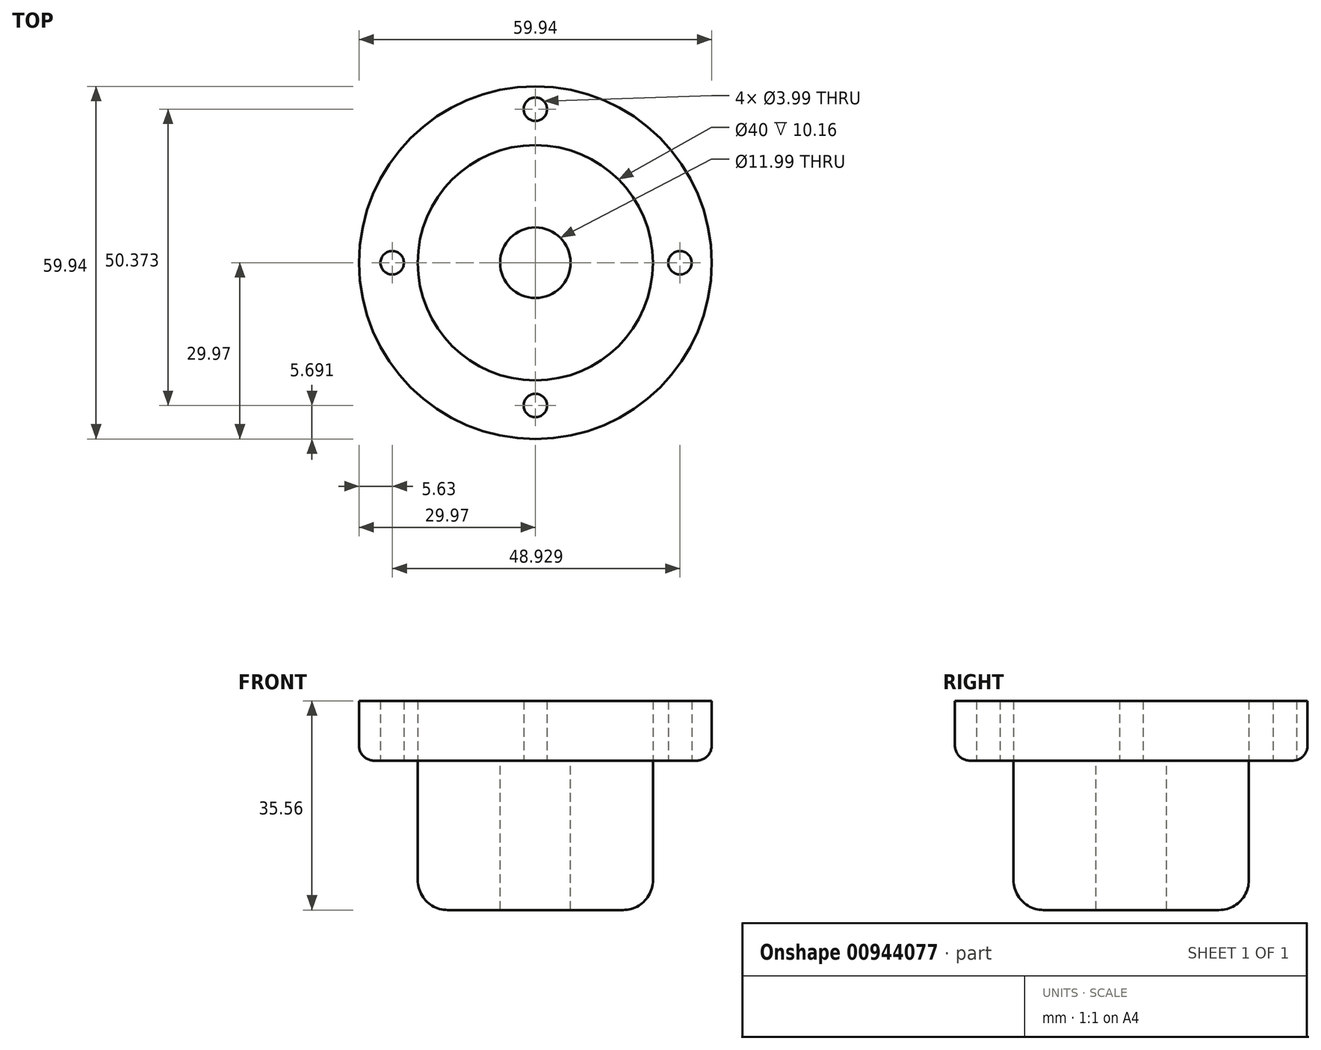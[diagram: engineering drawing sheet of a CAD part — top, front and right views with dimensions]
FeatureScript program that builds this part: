
annotation { "Feature Type Name" : "Feature", "Feature Type Description" : "" }
export const myFeature = defineFeature(function(context is Context, id is Id, definition is map)
    precondition{}
    {
        {
            var Q0;
            Q0=qCreatedBy(makeId("Top.planeOp"),FACE);
            var sketch = newSketch(context, id + "F0", { "sketchPlane" : qUnion([Q0])});
            skCircle(sketch, "E0", {"center": v(0, 0) * mm, "radius": 6 * mm});
            skCircle(sketch, "E1", {"center": v(0, 0) * mm, "radius": 20 * mm});
            skCircle(sketch, "E2", {"center": v(0, 0) * mm, "radius": 29.97 * mm});
            skPoint(sketch, "E3.center.orphan", {"position": v(0, -12.96) * mm});
            skPoint(sketch, "E4.center.orphan", {"position": v(-13.55, 0) * mm});
            skPoint(sketch, "E5.center.orphan", {"position": v(0, 13.55) * mm});
            skPoint(sketch, "E6.center.orphan", {"position": v(12.22, 0) * mm});
            skCircle(sketch, "E7", {"center": v(0, 26.1) * mm, "radius": 2 * mm});
            skCircle(sketch, "E8", {"center": v(24.59, 0) * mm, "radius": 2 * mm});
            skCircle(sketch, "E9", {"center": v(0, -24.28) * mm, "radius": 2 * mm});
            skCircle(sketch, "E10", {"center": v(-24.34, 0) * mm, "radius": 2 * mm});
            skSolve(sketch);
        }
        {
            var Q0;
            Q0=makeQuery(id+"F0.imprint","IMPRINT",FACE,{"disambiguationData":[TD([[makeQuery(id+"F0.imprint","IMPRINT",EDGE,{"derivedFrom":sQuery(id+"F0.wireOp",EDGE,"E0")}),-1.0]])]});
            extrude(context, id + "F1", {"entities" : qUnion([Q0]), "oppositeDirection" : true, "depth" : 25.4 * mm, "offsetDistance" : 25.4 * mm});
        }
        {
            var Q0;
            Q0 = qSketchRegion(id + "FecH7Nu9EQkDdAY_1", true);
            var Q1;
            Q1 = qSketchRegion(id + "F0", true);
            extrude(context, id + "F2", {"entities" : qUnion([Q0, Q1]), "depth" : 10.16 * mm, "offsetDistance" : 25.4 * mm});
        }
        {
            var Q0;
            Q0=makeQuery(id+"F1.opExtrude","CAP_EDGE",EDGE,{"disambiguationData":[OSD([sQuery(id+"F0.wireOp",EDGE,"E1")])],"isStart":false});
            fillet(context, id + "F3", {"entities" : qUnion([Q0]), "radius" : 5.08 * mm, "tangentPropagation" : true, "allowEdgeOverflow" : false});
        }
        {
            var Q0;
            Q0=makeQuery(id+"F2.opExtrude","CAP_EDGE",EDGE,{"disambiguationData":[OSD([sQuery(id+"F0.wireOp",EDGE,"E2")])],"isStart":true});
            fillet(context, id + "F4", {"entities" : qUnion([Q0]), "radius" : 2.54 * mm, "tangentPropagation" : true, "allowEdgeOverflow" : false});
        }
    });
